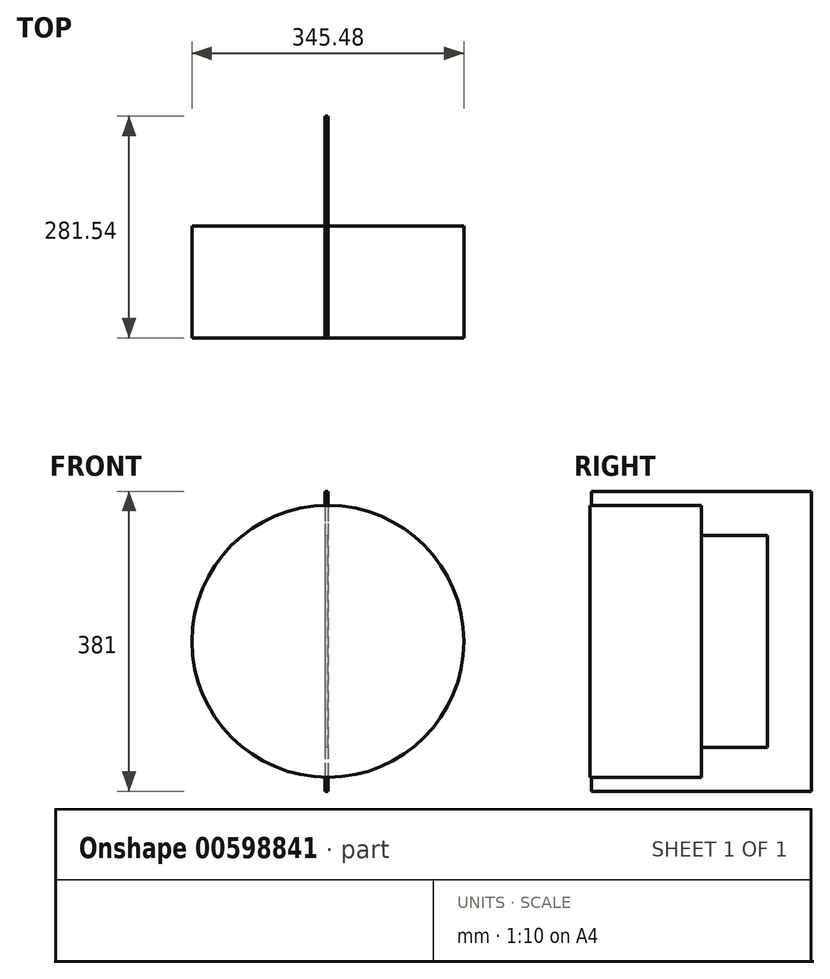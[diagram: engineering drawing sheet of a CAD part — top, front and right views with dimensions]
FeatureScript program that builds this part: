
annotation { "Feature Type Name" : "Feature", "Feature Type Description" : "" }
export const myFeature = defineFeature(function(context is Context, id is Id, definition is map)
    precondition{}
    {
        {
            var Q0;
            Q0=qCreatedBy(makeId("Right.planeOp"),FACE);
            var sketch = newSketch(context, id + "F0", { "sketchPlane" : qUnion([Q0])});
            skLineSegment(sketch, "E0.bottom", {"start": v(139.7, 190.5) * mm, "end": v(-139.7, 190.5) * mm});
            skLineSegment(sketch, "E0.top", {"start": v(139.7, -190.5) * mm, "end": v(-139.7, -190.5) * mm});
            skLineSegment(sketch, "E0.left", {"start": v(139.7, 190.5) * mm, "end": v(139.7, -190.5) * mm});
            skLineSegment(sketch, "E0.right", {"start": v(-139.7, 190.5) * mm, "end": v(-139.7, -190.5) * mm});
            skPoint(sketch, "E0.middle", {"position": v(0, 0) * mm});
            skSolve(sketch);
        }
        {
            var Q0;
            Q0=makeQuery(id+"F0.imprint","IMPRINT",FACE,{"disambiguationData":[TD([[makeQuery(id+"F0.imprint","IMPRINT",EDGE,{"derivedFrom":sQuery(id+"F0.wireOp",EDGE,"E0.bottom")}),1.0]])]});
            extrude(context, id + "F1", {"entities" : qUnion([Q0]), "oppositeDirection" : true, "depth" : 3.56 * mm, "offsetDistance" : 25.4 * mm});
        }
        {
            var Q0;
            Q0=makeQuery(id+"F1.opExtrude","CAP_FACE",FACE,{"disambiguationData":[OSD([sQuery(id+"F0.wireOp",EDGE,"E0.bottom"),sQuery(id+"F0.wireOp",EDGE,"E0.top"),sQuery(id+"F0.wireOp",EDGE,"E0.left"),sQuery(id+"F0.wireOp",EDGE,"E0.right")])],"isStart":false});
            var sketch = newSketch(context, id + "F2", { "sketchPlane" : qUnion([Q0])});
            skLineSegment(sketch, "E1.0", {"start": v(-83.82, -134.62) * mm, "end": v(83.82, -134.62) * mm});
            skLineSegment(sketch, "E1.1", {"start": v(-83.82, 134.62) * mm, "end": v(-83.82, -134.62) * mm});
            skLineSegment(sketch, "E1.2", {"start": v(83.82, 134.62) * mm, "end": v(-83.82, 134.62) * mm});
            skLineSegment(sketch, "E1.3", {"start": v(83.82, -134.62) * mm, "end": v(83.82, 134.62) * mm});
            skSolve(sketch);
        }
        {
            var Q0;
            Q0=makeQuery(id+"F2.imprint","IMPRINT",FACE,{"disambiguationData":[TD([[makeQuery(id+"F2.imprint","IMPRINT",EDGE,{"derivedFrom":sQuery(id+"F2.wireOp",EDGE,"E1.0")}),1.0]])]});
            extrude(context, id + "F3", {"entities" : qUnion([Q0]), "operationType" : NewBodyOperationType.REMOVE, "oppositeDirection" : true, "depth" : 56.4 * mm, "offsetDistance" : 25.4 * mm});
        }
        {
            var Q0;
            Q0=qCreatedBy(makeId("Front.planeOp"),FACE);
            var sketch = newSketch(context, id + "F4", { "sketchPlane" : qUnion([Q0])});
            skCircle(sketch, "E2", {"center": v(0, 0) * mm, "radius": 172.74 * mm});
            skSolve(sketch);
        }
        {
            var Q0;
            Q0=makeQuery(id+"F4.imprint","IMPRINT",FACE,{"disambiguationData":[TD([[makeQuery(id+"F4.imprint","IMPRINT",EDGE,{"derivedFrom":sQuery(id+"F4.wireOp",EDGE,"E2")}),1.0]])]});
            extrude(context, id + "F5", {"entities" : qUnion([Q0]), "operationType" : NewBodyOperationType.ADD, "depth" : 141.84 * mm, "offsetDistance" : 25.4 * mm});
        }
    });
